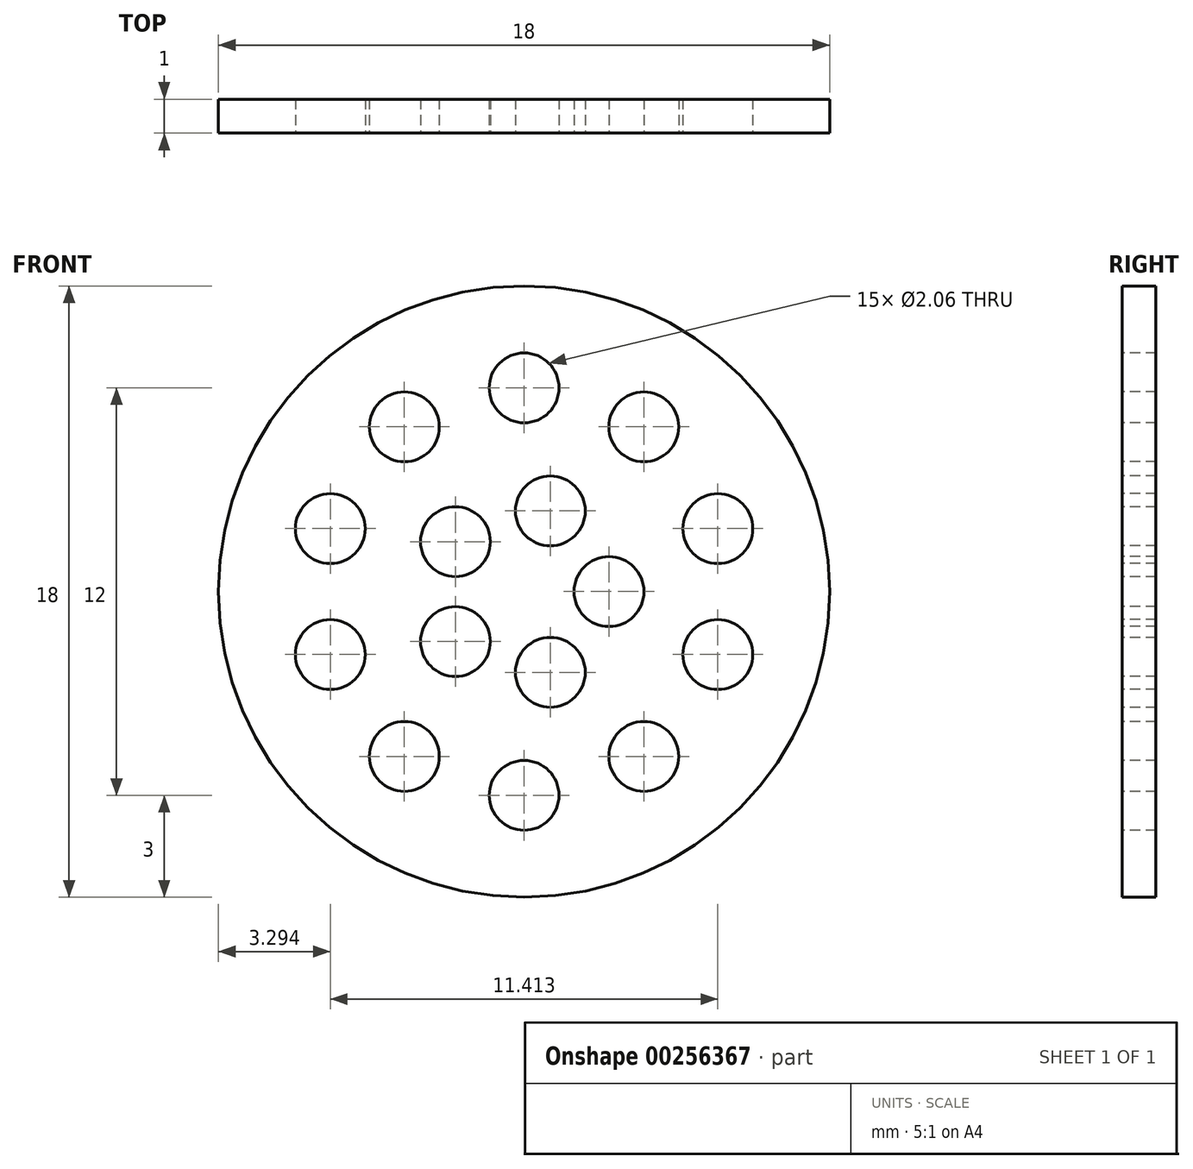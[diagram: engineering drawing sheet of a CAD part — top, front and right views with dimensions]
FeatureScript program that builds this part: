
annotation { "Feature Type Name" : "Feature", "Feature Type Description" : "" }
export const myFeature = defineFeature(function(context is Context, id is Id, definition is map)
    precondition{}
    {
        {
            var Q0;
            Q0=qCreatedBy(makeId("Front.planeOp"),FACE);
            var sketch = newSketch(context, id + "F0", { "sketchPlane" : qUnion([Q0])});
            skCircle(sketch, "E0", {"center": v(0, 0) * mm, "radius": 9 * mm});
            skSolve(sketch);
        }
        {
            var Q0;
            Q0=qSketchRegion(id+"F0",true);
            extrude(context, id + "F1", {"entities" : qUnion([Q0]), "depth" : 1 * mm});
        }
        {
            var Q0;
            Q0=makeQuery(id+"F1.opExtrude","CAP_FACE",FACE,{"disambiguationData":[OSD([sQuery(id+"F0.wireOp",EDGE,"E0")])],"isStart":false});
            var sketch = newSketch(context, id + "F2", { "sketchPlane" : qUnion([Q0])});
            skCircle(sketch, "E1", {"center": v(0, 0) * mm, "radius": 6 * mm});
            skCircle(sketch, "E2", {"center": v(0, 0) * mm, "radius": 2.5 * mm});
            skPoint(sketch, "E3", {"position": v(0, 6) * mm});
            skPoint(sketch, "E4.1.0", {"position": v(-3.53, 4.85) * mm});
            skPoint(sketch, "E4.2.0", {"position": v(-5.7, 1.85) * mm});
            skPoint(sketch, "E4.3.0", {"position": v(-5.7, -1.85) * mm});
            skPoint(sketch, "E4.4.0", {"position": v(-3.53, -4.85) * mm});
            skPoint(sketch, "E4.5.0", {"position": v(0, -6) * mm});
            skPoint(sketch, "E4.6.0", {"position": v(3.53, -4.85) * mm});
            skPoint(sketch, "E4.7.0", {"position": v(5.7, -1.85) * mm});
            skPoint(sketch, "E5.0.8.0", {"position": v(5.7, 1.85) * mm});
            skPoint(sketch, "E5.0.9.0", {"position": v(3.53, 4.85) * mm});
            skPoint(sketch, "E6", {"position": v(2.5, 0) * mm});
            skPoint(sketch, "E7.1.0", {"position": v(0.77, 2.38) * mm});
            skPoint(sketch, "E7.2.0", {"position": v(-2.02, 1.47) * mm});
            skPoint(sketch, "E7.3.0", {"position": v(-2.02, -1.47) * mm});
            skPoint(sketch, "E7.4.0", {"position": v(0.77, -2.38) * mm});
            skSolve(sketch);
        }
        {
            var Q0;
            Q0=sQuery(id+"F2.wireOp",VERTEX,"IZkkXyyh-uieR-OPkv-T1By-iHbS7jxYazU4.center");
            var Q1;
            Q1=sQuery(id+"F2.wireOp",VERTEX,"e5d7f120-e1ad-4062-a4dd-eb10c04244b4.1.0");
            var Q2;
            Q2=sQuery(id+"F2.wireOp",VERTEX,"a3fc0f77-ada5-4d6e-a54e-82b45d77d4ef");
            var Q3;
            Q3=sQuery(id+"F2.wireOp",VERTEX,"e5d7f120-e1ad-4062-a4dd-eb10c04244b4.15.0");
            var Q4;
            Q4=sQuery(id+"F2.wireOp",VERTEX,"e5d7f120-e1ad-4062-a4dd-eb10c04244b4.14.0");
            var Q5;
            Q5=sQuery(id+"F2.wireOp",VERTEX,"e5d7f120-e1ad-4062-a4dd-eb10c04244b4.13.0");
            var Q6;
            Q6=sQuery(id+"F2.wireOp",VERTEX,"e5d7f120-e1ad-4062-a4dd-eb10c04244b4.12.0");
            var Q7;
            Q7=sQuery(id+"F2.wireOp",VERTEX,"e5d7f120-e1ad-4062-a4dd-eb10c04244b4.11.0");
            var Q8;
            Q8=sQuery(id+"F2.wireOp",VERTEX,"e5d7f120-e1ad-4062-a4dd-eb10c04244b4.10.0");
            var Q9;
            Q9=sQuery(id+"F2.wireOp",VERTEX,"e5d7f120-e1ad-4062-a4dd-eb10c04244b4.9.0");
            var Q10;
            Q10=sQuery(id+"F2.wireOp",VERTEX,"e5d7f120-e1ad-4062-a4dd-eb10c04244b4.8.0");
            var Q11;
            Q11=sQuery(id+"F2.wireOp",VERTEX,"e5d7f120-e1ad-4062-a4dd-eb10c04244b4.7.0");
            var Q12;
            Q12=sQuery(id+"F2.wireOp",VERTEX,"e5d7f120-e1ad-4062-a4dd-eb10c04244b4.6.0");
            var Q13;
            Q13=sQuery(id+"F2.wireOp",VERTEX,"e5d7f120-e1ad-4062-a4dd-eb10c04244b4.5.0");
            var Q14;
            Q14=sQuery(id+"F2.wireOp",VERTEX,"e5d7f120-e1ad-4062-a4dd-eb10c04244b4.4.0");
            var Q15;
            Q15=sQuery(id+"F2.wireOp",VERTEX,"e5d7f120-e1ad-4062-a4dd-eb10c04244b4.3.0");
            var Q16;
            Q16=sQuery(id+"F2.wireOp",VERTEX,"e5d7f120-e1ad-4062-a4dd-eb10c04244b4.2.0");
            var Q17;
            Q17=sQuery(id+"F2.wireOp",VERTEX,"E4.1.0");
            var Q18;
            Q18=sQuery(id+"F2.wireOp",VERTEX,"E4.2.0");
            var Q19;
            Q19=sQuery(id+"F2.wireOp",VERTEX,"E4.3.0");
            var Q20;
            Q20=sQuery(id+"F2.wireOp",VERTEX,"E4.4.0");
            var Q21;
            Q21=sQuery(id+"F2.wireOp",VERTEX,"E4.5.0");
            var Q22;
            Q22=sQuery(id+"F2.wireOp",VERTEX,"E4.6.0");
            var Q23;
            Q23=sQuery(id+"F2.wireOp",VERTEX,"E4.7.0");
            var Q24;
            Q24=sQuery(id+"F2.wireOp",VERTEX,"E3");
            var Q25;
            Q25=sQuery(id+"F2.wireOp",VERTEX,"fe61b65a-4676-42ba-b70b-1be49e719168");
            var Q26;
            Q26=sQuery(id+"F2.wireOp",VERTEX,"41a6d257-8674-4c30-ae07-6221aaa3ded3.1.0");
            var Q27;
            Q27=sQuery(id+"F2.wireOp",VERTEX,"41a6d257-8674-4c30-ae07-6221aaa3ded3.2.0");
            var Q28;
            Q28=sQuery(id+"F2.wireOp",VERTEX,"41a6d257-8674-4c30-ae07-6221aaa3ded3.3.0");
            var Q29;
            Q29=sQuery(id+"F2.wireOp",VERTEX,"E7.2.0");
            var Q30;
            Q30=sQuery(id+"F2.wireOp",VERTEX,"E7.3.0");
            var Q31;
            Q31=sQuery(id+"F2.wireOp",VERTEX,"E7.4.0");
            var Q32;
            Q32=sQuery(id+"F2.wireOp",VERTEX,"E6");
            var Q33;
            Q33=sQuery(id+"F2.wireOp",VERTEX,"E7.1.0");
            var Q34;
            Q34=sQuery(id+"F2.wireOp",VERTEX,"E5.0.9.0");
            var Q35;
            Q35=sQuery(id+"F2.wireOp",VERTEX,"E5.0.8.0");
            var Q36;
            Q36=makeQuery(id+"F1.opExtrude","SWEPT_BODY",BODY,{"disambiguationData":[OSD([sQuery(id+"F0.wireOp",EDGE,"E0")])]});
            hole(context, id + "F3", {"style" : HoleStyle.SIMPLE, "endStyle" : HoleEndStyle.BLIND, "standardTappedOrClearance" : lookupTablePath({ "standard" : "ANSI", "fit" : "Normal (ASME)", "size" : "#1", "type" : "Clearance" }), "standardBlindInLast" : lookupTablePath({ "fit" : "Free", "standard" : "ANSI", "size" : "#1", "type" : "Clearance" }), "holeDiameter" : 2.06 * mm, "holeDepth" : 15 * mm, "tappedDepth" : 12 * mm, "tapClearance" : 3, "locations" : qUnion([Q0, Q1, Q2, Q3, Q4, Q5, Q6, Q7, Q8, Q9, Q10, Q11, Q12, Q13, Q14, Q15, Q16, Q17, Q18, Q19, Q20, Q21, Q22, Q23, Q24, Q25, Q26, Q27, Q28, Q29, Q30, Q31, Q32, Q33, Q34, Q35]), "scope" : qUnion([Q36])});
        }
    });
